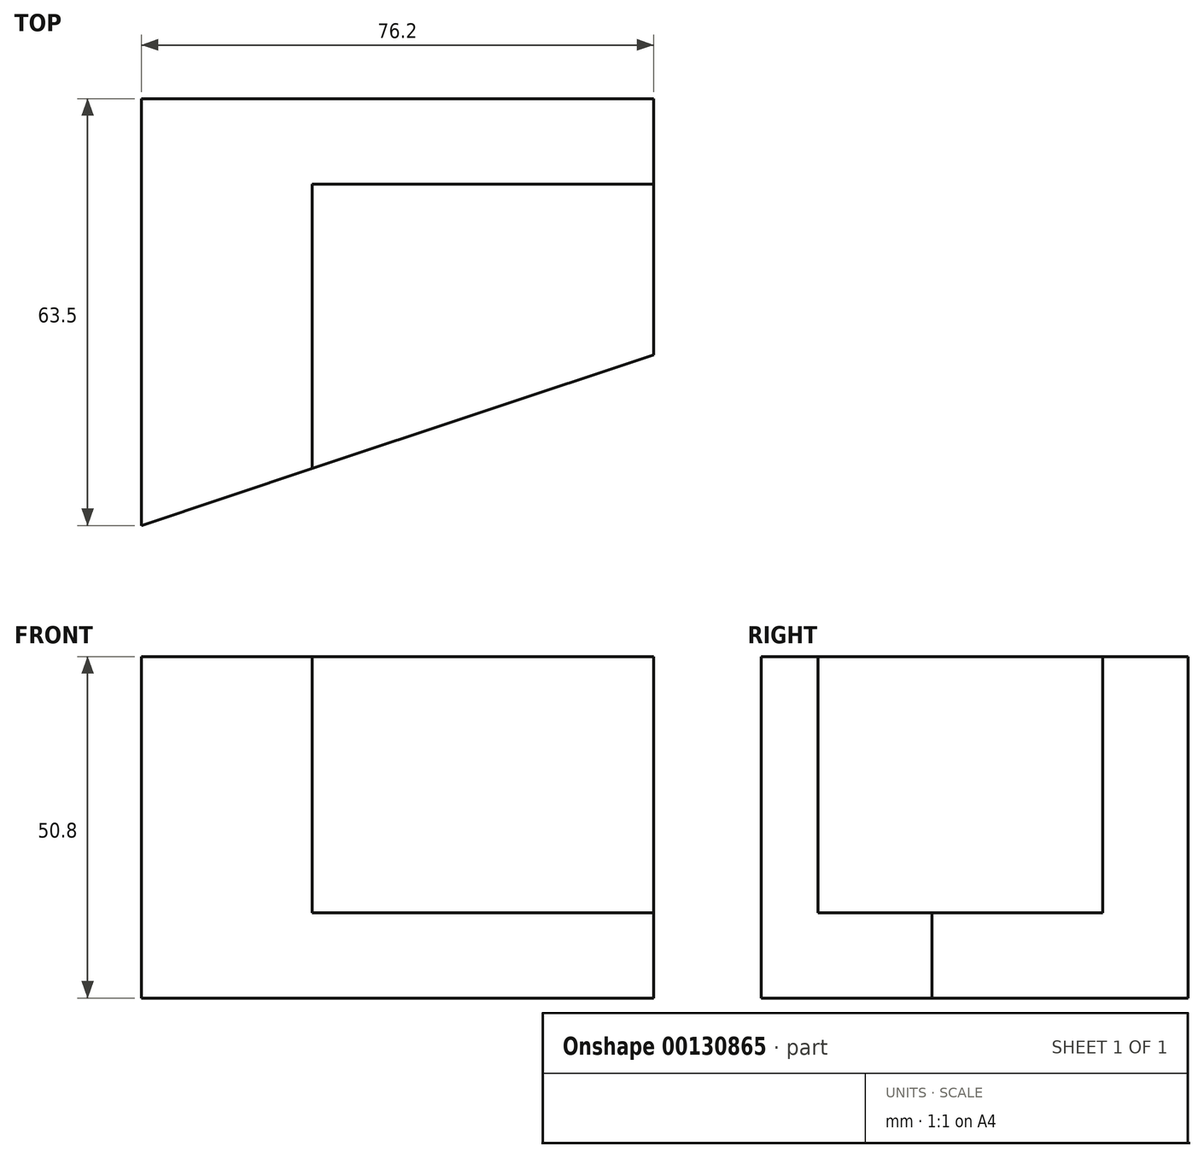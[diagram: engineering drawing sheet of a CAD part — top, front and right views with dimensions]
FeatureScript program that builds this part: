
annotation { "Feature Type Name" : "Feature", "Feature Type Description" : "" }
export const myFeature = defineFeature(function(context is Context, id is Id, definition is map)
    precondition{}
    {
        {
            var Q0;
            Q0=qCreatedBy(makeId("Top.planeOp"),FACE);
            var sketch = newSketch(context, id + "F0", { "sketchPlane" : qUnion([Q0])});
            skLineSegment(sketch, "E0", {"start": v(0, 0) * mm, "end": v(76.2, 0) * mm});
            skLineSegment(sketch, "E1", {"start": v(76.2, 0) * mm, "end": v(76.2, -38.1) * mm});
            skLineSegment(sketch, "E2", {"start": v(0, 0) * mm, "end": v(0, -63.5) * mm});
            skLineSegment(sketch, "E3", {"start": v(0, -63.5) * mm, "end": v(76.2, -38.1) * mm});
            skSolve(sketch);
        }
        {
            var Q0;
            Q0=makeQuery(id+"F0.imprint","IMPRINT",FACE,{"disambiguationData":[TD([[makeQuery(id+"F0.imprint","IMPRINT",EDGE,{"derivedFrom":sQuery(id+"F0.wireOp",EDGE,"E0")}),-1.0]])]});
            extrude(context, id + "F1", {"entities" : qUnion([Q0]), "depth" : 50.8 * mm});
        }
        {
            var Q0;
            Q0=makeQuery(id+"F1.opExtrude","CAP_FACE",FACE,{"disambiguationData":[OSD([sQuery(id+"F0.wireOp",EDGE,"E0"),sQuery(id+"F0.wireOp",EDGE,"E1"),sQuery(id+"F0.wireOp",EDGE,"E2"),sQuery(id+"F0.wireOp",EDGE,"E3")])],"isStart":false});
            var sketch = newSketch(context, id + "F2", { "sketchPlane" : qUnion([Q0])});
            skLineSegment(sketch, "E4", {"start": v(0, 0) * mm, "end": v(25.4, 0) * mm, "construction": true});
            skLineSegment(sketch, "E5", {"start": v(25.4, 0) * mm, "end": v(25.4, -12.7) * mm, "construction": true});
            skLineSegment(sketch, "E6", {"start": v(25.4, -12.7) * mm, "end": v(76.2, -12.7) * mm});
            skLineSegment(sketch, "E7", {"start": v(76.2, -12.7) * mm, "end": v(76.2, -38.1) * mm});
            skLineSegment(sketch, "E8", {"start": v(25.4, -12.7) * mm, "end": v(25.4, -55.03) * mm});
            skLineSegment(sketch, "E9", {"start": v(25.4, -55.03) * mm, "end": v(76.2, -38.1) * mm});
            skSolve(sketch);
        }
        {
            var Q0;
            Q0=makeQuery(id+"F2.imprint","IMPRINT",FACE,{"disambiguationData":[TD([[makeQuery(id+"F2.imprint","IMPRINT",EDGE,{"derivedFrom":sQuery(id+"F2.wireOp",EDGE,"E6")}),-1.0]])]});
            extrude(context, id + "F3", {"entities" : qUnion([Q0]), "operationType" : NewBodyOperationType.REMOVE, "oppositeDirection" : true, "depth" : 38.1 * mm});
        }
    });
